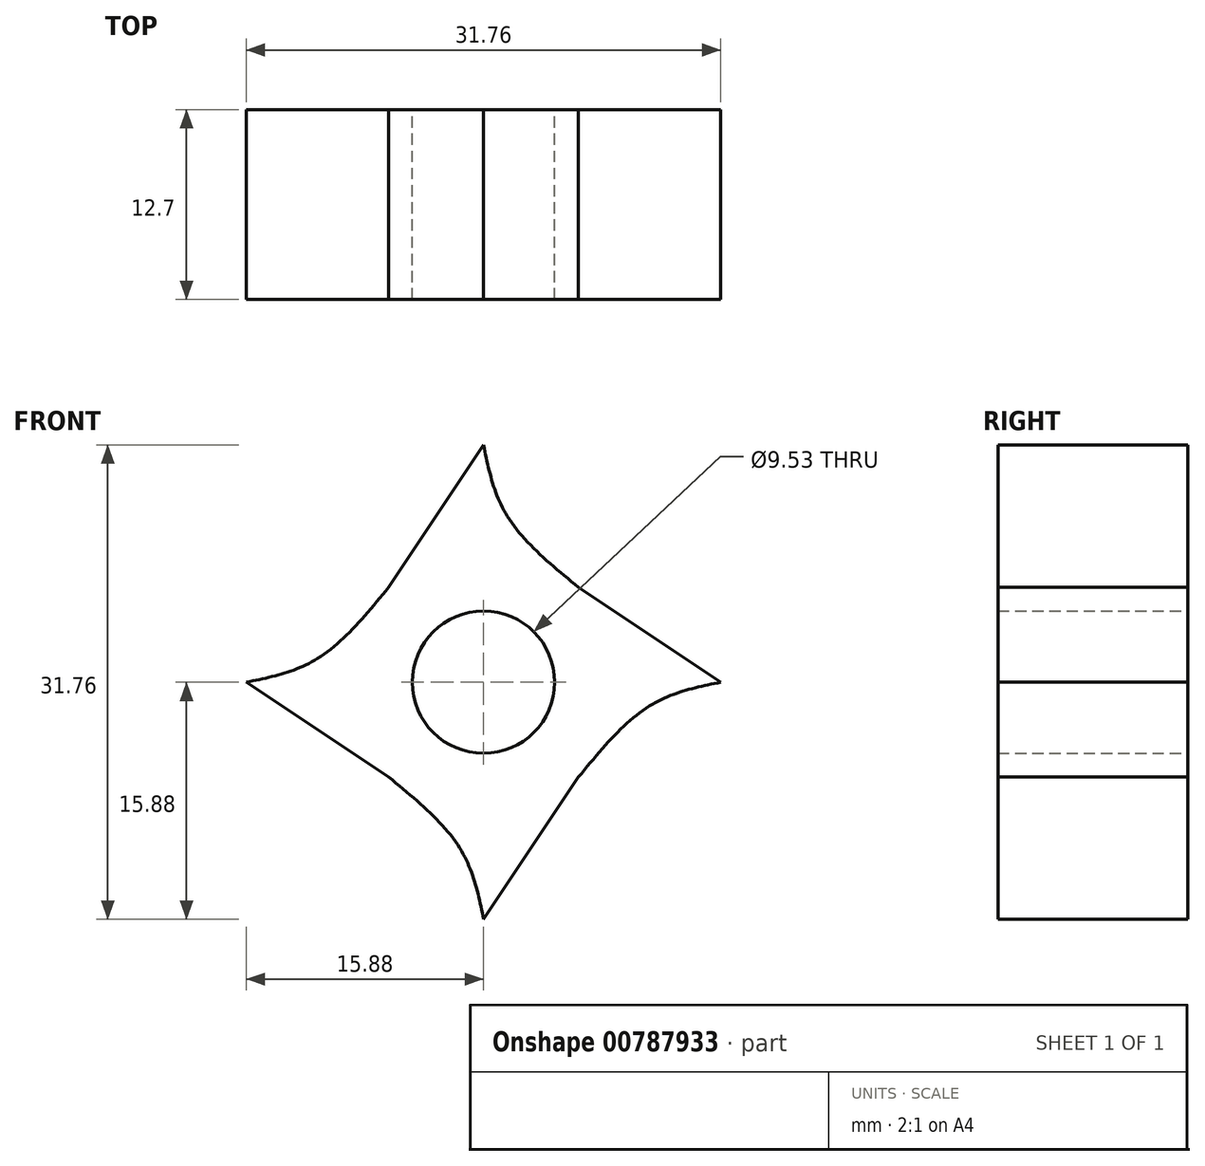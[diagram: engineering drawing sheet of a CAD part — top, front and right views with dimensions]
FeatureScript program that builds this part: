
annotation { "Feature Type Name" : "Feature", "Feature Type Description" : "" }
export const myFeature = defineFeature(function(context is Context, id is Id, definition is map)
    precondition{}
    {
        {
            var Q0;
            Q0=qCreatedBy(makeId("Front.planeOp"),FACE);
            var sketch = newSketch(context, id + "F0", { "sketchPlane" : qUnion([Q0])});
            skLineSegment(sketch, "E0.bottom", {"start": v(0, 0) * mm, "end": v(12.7, 0) * mm});
            skLineSegment(sketch, "E0.top", {"start": v(0, 12.7) * mm, "end": v(12.7, 12.7) * mm});
            skLineSegment(sketch, "E0.left", {"start": v(0, 0) * mm, "end": v(0, 12.7) * mm});
            skLineSegment(sketch, "E0.right", {"start": v(12.7, 0) * mm, "end": v(12.7, 12.7) * mm});
            skLineSegment(sketch, "E1", {"start": v(0, 6.35) * mm, "end": v(12.7, 6.35) * mm});
            skLineSegment(sketch, "E2", {"start": v(6.35, 12.7) * mm, "end": v(6.35, 0) * mm});
            skCircle(sketch, "E3", {"center": v(6.35, 6.35) * mm, "radius": 4.76 * mm});
            skLineSegment(sketch, "E4", {"start": v(6.35, 12.7) * mm, "end": v(12.7, 12.7) * mm});
            skLineSegment(sketch, "E5", {"start": v(6.35, 12.7) * mm, "end": v(6.35, 22.23) * mm});
            skLineSegment(sketch, "E6", {"start": v(0, 12.7) * mm, "end": v(6.35, 12.7) * mm});
            skLineSegment(sketch, "E7", {"start": v(6.35, 17.46) * mm, "end": v(6.35, 12.7) * mm});
            skLineSegment(sketch, "E8", {"start": v(3.17, 12.7) * mm, "end": v(6.35, 12.7) * mm});
            skLineSegment(sketch, "E9", {"start": v(9.52, 12.7) * mm, "end": v(6.35, 12.7) * mm});
            skLineSegment(sketch, "E10", {"start": v(6.35, 17.46) * mm, "end": v(7.94, 17.46) * mm});
            skPoint(sketch, "E10.endSnap0", {"position": v(7.94, 12.7) * mm});
            skFitSpline(sketch, "E11", {"points": [v(6.35, 22.22) * mm, v(7.94, 17.46) * mm, v(12.7, 12.7) * mm], "startDerivative": vector(2.16, -10.6) * mm, "endDerivative": vector(10.34, -8.5) * mm});
            skLineSegment(sketch, "E12", {"start": v(0, 12.7) * mm, "end": v(6.35, 22.23) * mm});
            skLineSegment(sketch, "E13", {"start": v(12.7, 6.35) * mm, "end": v(22.23, 6.35) * mm});
            skLineSegment(sketch, "E14", {"start": v(12.7, 12.7) * mm, "end": v(22.23, 6.35) * mm});
            skLineSegment(sketch, "E15", {"start": v(12.7, 6.35) * mm, "end": v(12.7, 0) * mm});
            skLineSegment(sketch, "E16", {"start": v(12.7, 3.17) * mm, "end": v(12.7, 6.35) * mm});
            skLineSegment(sketch, "E17", {"start": v(12.7, 6.35) * mm, "end": v(17.46, 6.35) * mm});
            skLineSegment(sketch, "E18", {"start": v(17.46, 6.35) * mm, "end": v(17.46, 4.76) * mm});
            skPoint(sketch, "E18.endSnap0", {"position": v(12.7, 4.76) * mm});
            skFitSpline(sketch, "E19", {"points": [v(22.23, 6.35) * mm, v(17.46, 4.76) * mm, v(12.7, 0) * mm], "startDerivative": vector(-10.6, -2.16) * mm, "endDerivative": vector(-8.5, -10.34) * mm});
            skLineSegment(sketch, "E20", {"start": v(6.35, 0) * mm, "end": v(6.35, -9.53) * mm});
            skLineSegment(sketch, "E21", {"start": v(6.35, -9.53) * mm, "end": v(12.7, 0) * mm});
            skLineSegment(sketch, "E22", {"start": v(6.35, 0) * mm, "end": v(0, 0) * mm});
            skLineSegment(sketch, "E23", {"start": v(3.18, 0) * mm, "end": v(6.35, 0) * mm});
            skLineSegment(sketch, "E24", {"start": v(6.35, -4.76) * mm, "end": v(4.76, -4.76) * mm});
            skPoint(sketch, "E24.endSnap0", {"position": v(4.76, 0) * mm});
            skFitSpline(sketch, "E25", {"points": [v(0, 0) * mm, v(4.76, -4.76) * mm, v(6.35, -9.53) * mm], "startDerivative": vector(10.34, -8.5) * mm, "endDerivative": vector(2.16, -10.6) * mm});
            skLineSegment(sketch, "E26", {"start": v(0, 6.35) * mm, "end": v(-9.53, 6.35) * mm});
            skLineSegment(sketch, "E27", {"start": v(-9.53, 6.35) * mm, "end": v(0, 0) * mm});
            skLineSegment(sketch, "E28", {"start": v(0, 6.35) * mm, "end": v(0, 12.7) * mm});
            skLineSegment(sketch, "E29", {"start": v(0, 9.52) * mm, "end": v(0, 6.35) * mm});
            skLineSegment(sketch, "E30", {"start": v(-4.76, 6.35) * mm, "end": v(-4.76, 7.94) * mm});
            skPoint(sketch, "E30.endSnap0", {"position": v(0, 7.94) * mm});
            skFitSpline(sketch, "E31", {"points": [v(-9.53, 6.35) * mm, v(-4.76, 7.94) * mm, v(0, 12.7) * mm], "startDerivative": vector(10.6, 2.16) * mm, "endDerivative": vector(8.5, 10.34) * mm});
            skSolve(sketch);
        }
        {
            var Q0;
            Q0=qSketchRegion(id+"F0",true);
            extrude(context, id + "F1", {"entities" : qUnion([Q0]), "depth" : 12.7 * mm, "offsetDistance" : 25.4 * mm});
        }
    });
